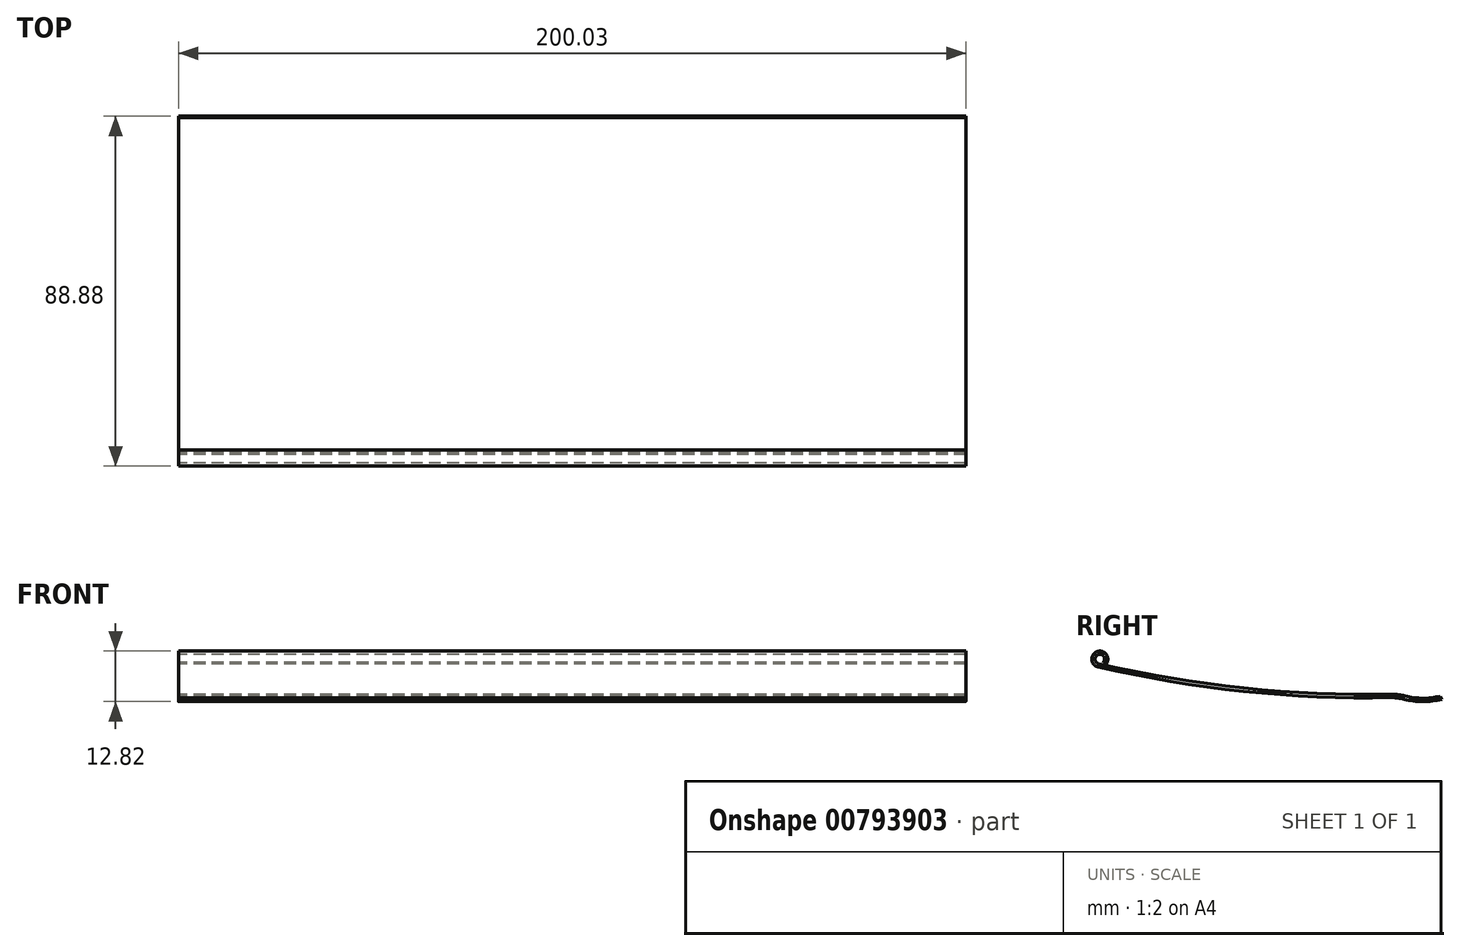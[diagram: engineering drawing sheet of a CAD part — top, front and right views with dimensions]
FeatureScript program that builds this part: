
annotation { "Feature Type Name" : "Feature", "Feature Type Description" : "" }
export const myFeature = defineFeature(function(context is Context, id is Id, definition is map)
    precondition{}
    {
        {
            var Q0;
            Q0=qCreatedBy(makeId("Right.planeOp"),FACE);
            var sketch = newSketch(context, id + "F0", { "sketchPlane" : qUnion([Q0])});
            skArc(sketch, "E0", {"start": v(-4.76, 12.3) * mm, "mid": v(0, 11.7) * mm, "end": v(4.76, 12.3) * mm});
            skArc(sketch, "E1", {"start": v(-4.76, 12.3) * mm, "mid": v(-6.45, 12.61) * mm, "end": v(-8.17, 12.7) * mm});
            skArc(sketch, "E2", {"start": v(-8.17, 12.7) * mm, "mid": v(-45.6, 14.31) * mm, "end": v(-82.55, 20.5) * mm});
            skArc(sketch, "E3.0", {"start": v(-8.19, 13.52) * mm, "mid": v(-45.52, 15.13) * mm, "end": v(-82.36, 21.3) * mm});
            skArc(sketch, "E4.0", {"start": v(-4.56, 13.1) * mm, "mid": v(-6.36, 13.43) * mm, "end": v(-8.19, 13.52) * mm});
            skArc(sketch, "E5.0", {"start": v(-4.56, 13.1) * mm, "mid": v(-0.06, 12.52) * mm, "end": v(4.44, 13.07) * mm});
            skLineSegment(sketch, "E6", {"start": v(4.44, 13.07) * mm, "end": v(4.76, 12.3) * mm});
            skArc(sketch, "E7", {"start": v(-82.55, 20.5) * mm, "mid": v(-82.79, 24.4) * mm, "end": v(-80.47, 21.26) * mm});
            skArc(sketch, "E8", {"start": v(-82.36, 21.3) * mm, "mid": v(-82.45, 23.63) * mm, "end": v(-81.2, 21.66) * mm});
            skLineSegment(sketch, "E9", {"start": v(-81.2, 21.66) * mm, "end": v(-80.47, 21.26) * mm});
            skSolve(sketch);
        }
        {
            var Q0;
            Q0=qSketchRegion(id+"F0",true);
            extrude(context, id + "F1", {"entities" : qUnion([Q0]), "depth" : 200.02 * mm, "offsetDistance" : 25.4 * mm});
        }
    });
